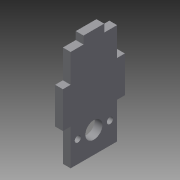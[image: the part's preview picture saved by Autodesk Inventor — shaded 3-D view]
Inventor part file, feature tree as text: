
AUTODESK INVENTOR PART (.ipt)
format: ipt  version: 2013 (Build 170138000, 138)  size: 118,784 bytes
history: native  units: in
note: dims shown in document units (in); Inventor stores cm internally (conversion verified against a paired STEP export)
features: extrude x3, sketch x3
ambient origin geometry x8: Origin, YZ Plane, XZ Plane, XY Plane, X Axis, Y Axis, Z Axis, Center Point
bodies: Solid1 (feature_tree)
feature tree (6):
  extrude  "Extrusion1"  Depth=0.75in
  extrude  "Extrusion2"  TaperAngle=0.0deg  [1 undecoded]
  extrude  "Extrusion3"  Depth=0.125in
  sketch  "Sketch1"  dims[d0=1.625in d1=0.75in]
  sketch  "Sketch2"  dims[d2=0.125in d3=0.0in]
  sketch  "Sketch3"  dims[d4=0.3333in d5=0.125in d6=0.2083in d7=0.125in d8=0.5833in d9=0.125in d10=0.5833in d11=0.5833in d12=0.125in d13=0.0in d14=0.276in d15=0.5in d16=0.35in d17=0.07in d18=0.07in d19=0.518in d20=0.259in d21=0.125in d22=0.0in]
note: 1 required parameter value undecoded (feature->parameter linkage not recoverable at this tier; creation-order binding heuristic only, values carry confidence <= 0.55)
